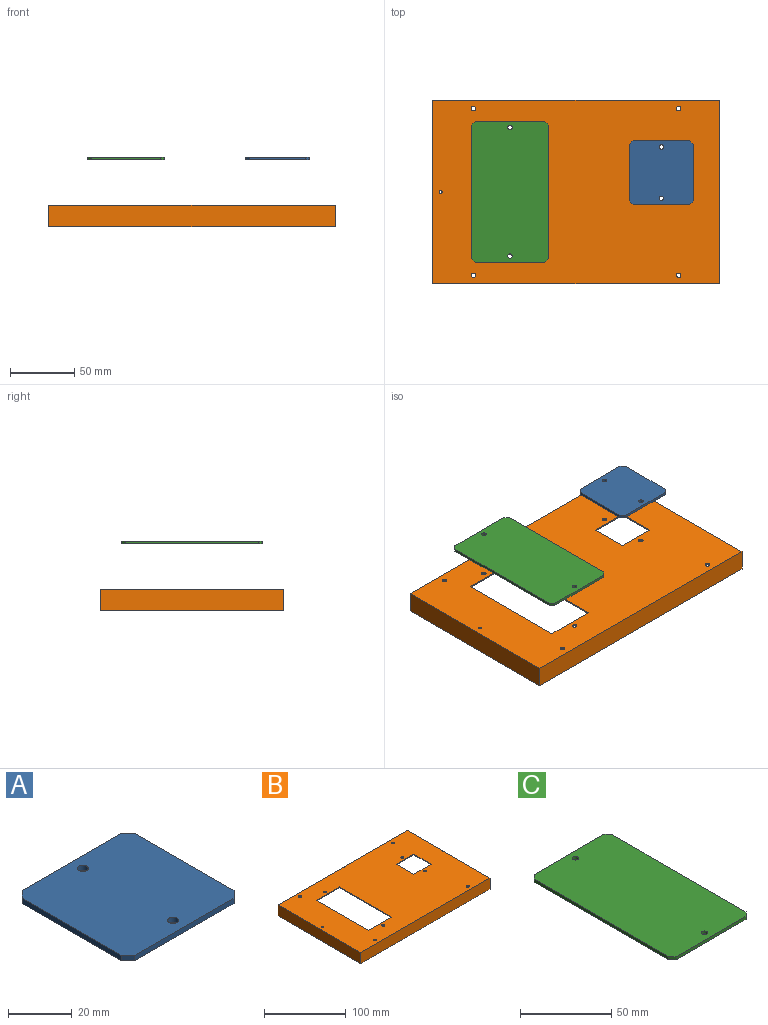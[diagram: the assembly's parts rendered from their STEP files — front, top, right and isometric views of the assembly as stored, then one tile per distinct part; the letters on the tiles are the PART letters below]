
ASSEMBLY  parts=3 mates=5
PART A: 12 faces, bbox 50x50x2 mm
  f0: plane 44x2mm, normal (0,1,0), area 88mm2, adj f4,f5,f8,f9
  f1: plane 44x2mm, normal (-1,0,0), area 88mm2, adj f4,f5,f8,f11
  f2: plane 44x2mm, normal (0,-1,0), area 88mm2, adj f4,f5,f10,f11
  f3: plane 44x2mm, normal (1,0,0), area 88mm2, adj f4,f5,f9,f10
  f4: plane 50x50mm, normal (0,0,1), area 2462.8mm2, adj f0,f1,f2,f3,f6,f7,f8,f9
  f5: plane 50x50mm, normal (0,0,-1), area 2462.8mm2, adj f0,f1,f2,f3,f6,f7,f8,f9
  f6: cylinder r=1.75mm len=3.5mm, axis (0,0,-1), area 22mm2, adj f4,f5
  f7: cylinder r=1.75mm len=3.5mm, axis (0,0,-1), area 22mm2, adj f4,f5
  f8: plane 3x3mm, normal (-0.71,0.71,0), area 8.5mm2, adj f0,f1,f4,f5
  f9: plane 3x3mm, normal (0.71,0.71,0), area 8.5mm2, adj f0,f3,f4,f5
  f10: plane 3x3mm, normal (0.71,-0.71,0), area 8.5mm2, adj f2,f3,f4,f5
  f11: plane 3x3mm, normal (-0.71,-0.71,0), area 8.5mm2, adj f1,f2,f4,f5
PART B: 28 faces, bbox 223x143x16.5 mm
  f0: plane 223x143mm, normal (0,0,-1), area 728mm2, adj f1,f2,f3,f4,f6,f7,f8,f9
  f1: plane 223x16.5mm, normal (0,1,0), area 3679.5mm2, adj f0,f2,f4,f5
  f2: plane 143x16.5mm, normal (-1,0,0), area 2359.5mm2, adj f0,f1,f3,f5
  f3: plane 223x16.5mm, normal (0,-1,0), area 3679.5mm2, adj f0,f2,f4,f5
  f4: plane 143x16.5mm, normal (1,0,0), area 2359.5mm2, adj f0,f1,f3,f5
  f5: plane 223x143mm, normal (0,0,1), area 27307.1mm2, adj f1,f2,f3,f4,f11,f12,f13,f14
  f6: plane 221x15.5mm, normal (0,-1,0), area 3425.5mm2, adj f0,f7,f9,f10
  f7: plane 141x15.5mm, normal (1,0,0), area 2185.5mm2, adj f0,f6,f8,f10
  f8: plane 221x15.5mm, normal (0,1,0), area 3425.5mm2, adj f0,f7,f9,f10
  f9: plane 141x15.5mm, normal (-1,0,0), area 2185.5mm2, adj f0,f6,f8,f10
  f10: plane 221x141mm, normal (0,0,-1), area 26579.1mm2, adj f6,f7,f8,f9,f11,f12,f13,f14
  f11: plane 30x1mm, normal (-1,0,0), area 30mm2, adj f5,f10,f12,f13
  f12: plane 30x1mm, normal (0,1,0), area 30mm2, adj f5,f10,f11,f14
  f13: plane 30x1mm, normal (0,-1,0), area 30mm2, adj f5,f10,f11,f14
  f14: plane 30x1mm, normal (1,0,0), area 30mm2, adj f5,f10,f12,f13
  f15: plane 90x1mm, normal (1,0,0), area 90mm2, adj f5,f10,f16,f17
  f16: plane 40x1mm, normal (0,-1,0), area 40mm2, adj f5,f10,f15,f18
  f17: plane 40x1mm, normal (0,1,0), area 40mm2, adj f5,f10,f15,f18
  f18: plane 90x1mm, normal (-1,0,0), area 90mm2, adj f5,f10,f16,f17
  f19: cylinder r=1.75mm len=3.5mm, axis (0,0,1), area 11mm2, adj f5,f10
  f20: cylinder r=1.75mm len=3.5mm, axis (0,0,1), area 11mm2, adj f5,f10
  f21: cylinder r=1.75mm len=3.5mm, axis (0,0,1), area 11mm2, adj f5,f10
  f22: cylinder r=1.75mm len=3.5mm, axis (0,0,1), area 11mm2, adj f5,f10
  f23: cylinder r=1.75mm len=3.5mm, axis (0,0,1), area 11mm2, adj f5,f10
  f24: cylinder r=1.75mm len=3.5mm, axis (0,0,1), area 11mm2, adj f5,f10
  f25: cylinder r=1.75mm len=3.5mm, axis (0,0,1), area 11mm2, adj f5,f10
  f26: cylinder r=1.75mm len=3.5mm, axis (0,0,1), area 11mm2, adj f5,f10
  f27: cylinder r=1.25mm len=2.5mm, axis (0,0,1), area 7.9mm2, adj f5,f10
PART C: 12 faces, bbox 60x110x2 mm
  f0: plane 54x2mm, normal (0,1,0), area 108mm2, adj f4,f5,f6,f7
  f1: plane 104x2mm, normal (-1,0,0), area 208mm2, adj f4,f5,f6,f9
  f2: plane 54x2mm, normal (0,-1,0), area 108mm2, adj f4,f5,f8,f9
  f3: plane 104x2mm, normal (1,0,0), area 208mm2, adj f4,f5,f7,f8
  f4: plane 110x60mm, normal (0,0,1), area 6562.8mm2, adj f0,f1,f2,f3,f6,f7,f8,f9
  f5: plane 110x60mm, normal (0,0,-1), area 6562.8mm2, adj f0,f1,f2,f3,f6,f7,f8,f9
  f6: plane 3x3mm, normal (-0.71,0.71,0), area 8.5mm2, adj f0,f1,f4,f5
  f7: plane 3x3mm, normal (0.71,0.71,0), area 8.5mm2, adj f0,f3,f4,f5
  f8: plane 3x3mm, normal (0.71,-0.71,0), area 8.5mm2, adj f2,f3,f4,f5
  f9: plane 3x3mm, normal (-0.71,-0.71,0), area 8.5mm2, adj f1,f2,f4,f5
  f10: cylinder r=1.75mm len=3.5mm, axis (0,0,1), area 22mm2, adj f4,f5
  f11: cylinder r=1.75mm len=3.5mm, axis (0,0,1), area 22mm2, adj f4,f5
PLACE A t=(166.8,41.02,67.45)mm
PLACE B t=(-11.2,97.52,32.01)mm
PLACE C t=(48.8,26.02,67.45)mm
MATE slider B.f22 <-> C.f10  axis (0,0,1) through (48.8,-23.98,32.01)mm
MATE slider B.f20 <-> A.f7  axis (0,0,1) through (166.8,61.02,32.01)mm
MATE planar C.f5 <-> A.f5  axis (0,0,-1) through (48.8,26.02,67.45)mm
MATE slider B.f21 <-> A.f6  axis (0,0,1) through (166.8,21.02,32.01)mm
MATE slider B.f26 <-> C.f11  axis (0,0,1) through (48.8,76.02,32.01)mm
